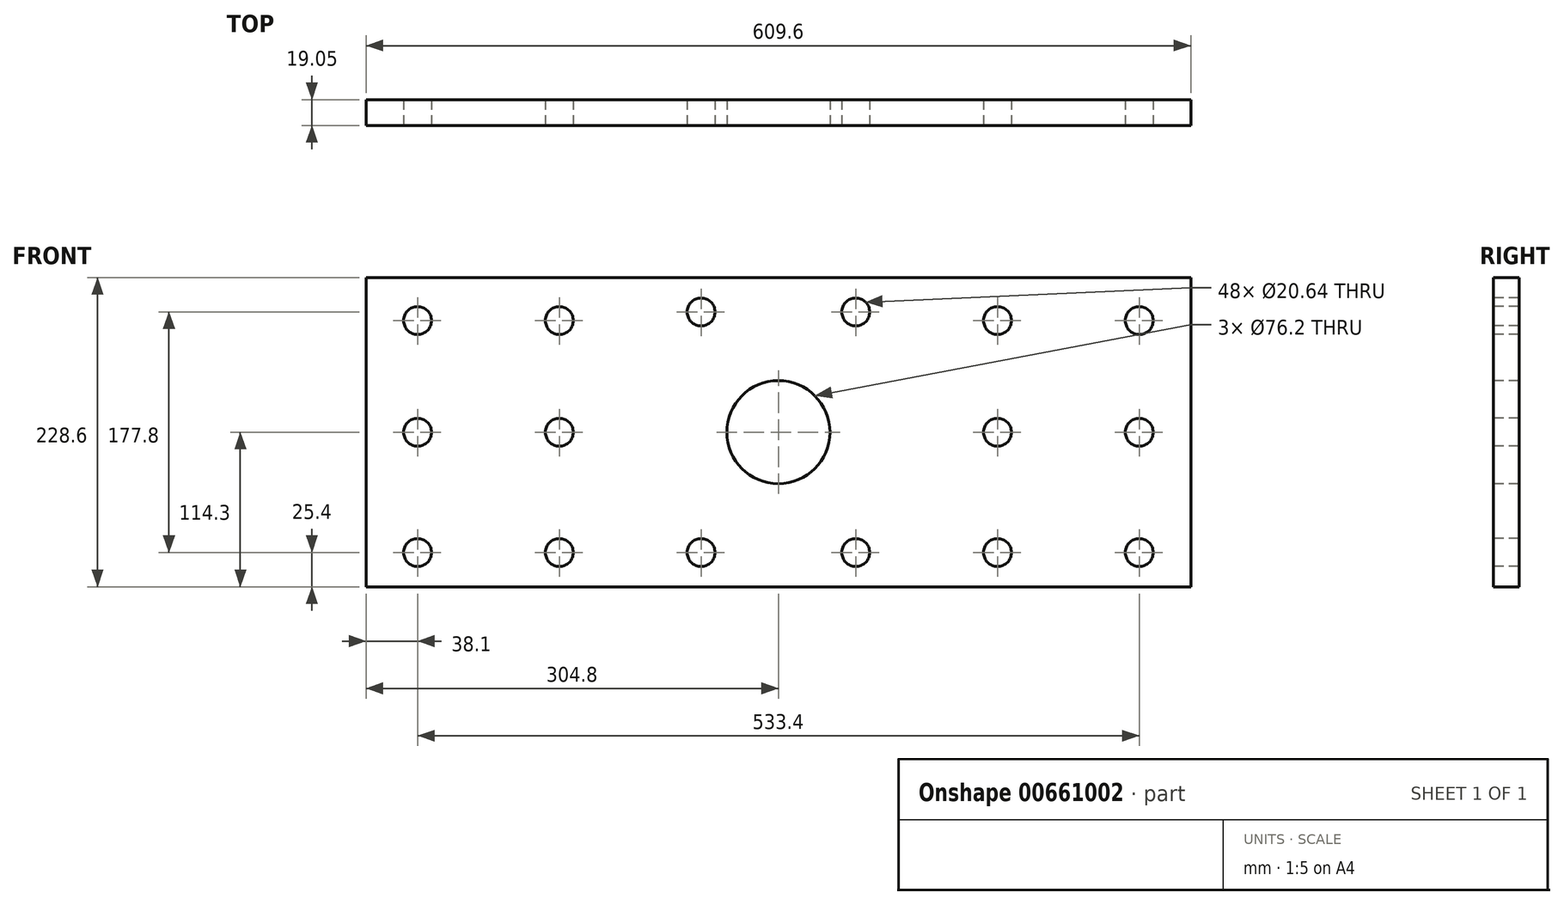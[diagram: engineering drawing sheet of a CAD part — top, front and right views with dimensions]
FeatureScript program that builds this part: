
annotation { "Feature Type Name" : "Feature", "Feature Type Description" : "" }
export const myFeature = defineFeature(function(context is Context, id is Id, definition is map)
    precondition{}
    {
        {
            var Q0;
            Q0=qCreatedBy(makeId("Front.planeOp"),FACE);
            var sketch = newSketch(context, id + "F0", { "sketchPlane" : qUnion([Q0])});
            skLineSegment(sketch, "E0", {"start": v(0, 0) * mm, "end": v(-609.6, 0) * mm, "construction": true});
            skLineSegment(sketch, "E1", {"start": v(0, 0) * mm, "end": v(0, 38.1) * mm, "construction": true});
            skCircle(sketch, "E2", {"center": v(0, 38.1) * mm, "radius": 38.1 * mm});
            skArc(sketch, "E3", {"start": v(-31.6, 85.72) * mm, "mid": v(0, -19.05) * mm, "end": v(31.6, 85.72) * mm});
            skCircle(sketch, "E4", {"center": v(161.93, 38.1) * mm, "radius": 10.32 * mm});
            skCircle(sketch, "E5", {"center": v(266.7, 38.1) * mm, "radius": 10.32 * mm});
            skCircle(sketch, "E6", {"center": v(161.93, -50.8) * mm, "radius": 10.32 * mm});
            skCircle(sketch, "E7", {"center": v(266.7, -50.8) * mm, "radius": 10.32 * mm});
            skCircle(sketch, "E8", {"center": v(57.15, 127) * mm, "radius": 10.32 * mm});
            skCircle(sketch, "E9", {"center": v(161.93, 120.65) * mm, "radius": 10.32 * mm});
            skCircle(sketch, "E10", {"center": v(266.7, 120.65) * mm, "radius": 10.32 * mm});
            skCircle(sketch, "E11", {"center": v(57.15, -50.8) * mm, "radius": 10.32 * mm});
            skLineSegment(sketch, "E12", {"start": v(0, 0) * mm, "end": v(0, 368.3) * mm, "construction": true});
            skCircle(sketch, "E13.MirrorC", {"center": v(-57.15, 127) * mm, "radius": 10.32 * mm});
            skCircle(sketch, "E14.MirrorC", {"center": v(-161.93, 120.65) * mm, "radius": 10.32 * mm});
            skCircle(sketch, "E15.MirrorC", {"center": v(-266.7, 120.65) * mm, "radius": 10.32 * mm});
            skCircle(sketch, "E16.MirrorC", {"center": v(-266.7, 38.1) * mm, "radius": 10.32 * mm});
            skCircle(sketch, "E17.MirrorC", {"center": v(-161.93, 38.1) * mm, "radius": 10.32 * mm});
            skCircle(sketch, "E18.MirrorC", {"center": v(-266.7, -50.8) * mm, "radius": 10.32 * mm});
            skCircle(sketch, "E19.MirrorC", {"center": v(-161.93, -50.8) * mm, "radius": 10.32 * mm});
            skCircle(sketch, "E20.MirrorC", {"center": v(-57.15, -50.8) * mm, "radius": 10.32 * mm});
            skLineSegment(sketch, "E21.bottom", {"start": v(304.8, 152.4) * mm, "end": v(-304.8, 152.4) * mm});
            skLineSegment(sketch, "E21.top", {"start": v(304.8, -76.2) * mm, "end": v(-304.8, -76.2) * mm});
            skLineSegment(sketch, "E21.left", {"start": v(304.8, 152.4) * mm, "end": v(304.8, 95.25) * mm});
            skLineSegment(sketch, "E21.right", {"start": v(-304.8, 152.4) * mm, "end": v(-304.8, -76.2) * mm});
            skLineSegment(sketch, "E22", {"start": v(0, 0) * mm, "end": v(609.6, 0) * mm, "construction": true});
            skLineSegment(sketch, "E23", {"start": v(0, 0) * mm, "end": v(0, 85.73) * mm, "construction": true});
            skLineSegment(sketch, "E24", {"start": v(0, 85.73) * mm, "end": v(31.6, 85.73) * mm});
            skLineSegment(sketch, "E25", {"start": v(0, 85.73) * mm, "end": v(-508, 85.73) * mm});
            skLineSegment(sketch, "E26", {"start": v(0, 85.73) * mm, "end": v(0, 95.25) * mm, "construction": true});
            skLineSegment(sketch, "E27", {"start": v(0, 95.25) * mm, "end": v(533.4, 95.25) * mm});
            skLineSegment(sketch, "E28", {"start": v(0, 95.25) * mm, "end": v(-508, 95.25) * mm});
            skLineSegment(sketch, "E29.left", {"start": v(660.4, -107.95) * mm, "end": v(660.4, 107.95) * mm});
            skLineSegment(sketch, "E29.right", {"start": v(558.8, -107.95) * mm, "end": v(558.8, 107.95) * mm});
            skLineSegment(sketch, "E30", {"start": v(660.4, 107.95) * mm, "end": v(676.27, 107.95) * mm});
            skLineSegment(sketch, "E31", {"start": v(676.27, 107.95) * mm, "end": v(676.27, 73.03) * mm});
            skLineSegment(sketch, "E32", {"start": v(676.27, -107.95) * mm, "end": v(660.4, -107.95) * mm});
            skLineSegment(sketch, "E33", {"start": v(558.8, 107.95) * mm, "end": v(542.92, 107.95) * mm});
            skLineSegment(sketch, "E34", {"start": v(542.92, 107.95) * mm, "end": v(542.92, 104.78) * mm});
            skLineSegment(sketch, "E35", {"start": v(542.92, -107.95) * mm, "end": v(558.8, -107.95) * mm});
            skLineSegment(sketch, "E36", {"start": v(0, 0) * mm, "end": v(0, -165.1) * mm, "construction": true});
            skLineSegment(sketch, "E37", {"start": v(0, -165.1) * mm, "end": v(685.18, -165.1) * mm});
            skLineSegment(sketch, "E38", {"start": v(0, 368.3) * mm, "end": v(152.4, 368.3) * mm, "construction": true});
            skCircle(sketch, "E39", {"center": v(152.4, 368.3) * mm, "radius": 11.9 * mm});
            skCircle(sketch, "E40", {"center": v(152.4, 368.3) * mm, "radius": 25.4 * mm});
            skLineSegment(sketch, "E41.bottom", {"start": v(609.6, 0) * mm, "end": v(671.5, 0) * mm, "construction": true});
            skLineSegment(sketch, "E41.top", {"start": v(609.6, 120.65) * mm, "end": v(671.5, 120.65) * mm, "construction": true});
            skLineSegment(sketch, "E41.left", {"start": v(609.6, 0) * mm, "end": v(609.6, 120.65) * mm, "construction": true});
            skLineSegment(sketch, "E41.right", {"start": v(671.5, 0) * mm, "end": v(671.5, 120.65) * mm, "construction": true});
            skArc(sketch, "E42", {"start": v(746.55, 107.42) * mm, "mid": v(736.68, 160.14) * mm, "end": v(694.5, 193.3) * mm});
            skLineSegment(sketch, "E43", {"start": v(700.81, -151.98) * mm, "end": v(746.55, 107.42) * mm});
            skPoint(sketch, "E44.visualSharp", {"position": v(698.5, -165.1) * mm});
            skArc(sketch, "E44.filletArc", {"start": v(685.18, -165.1) * mm, "mid": v(695.38, -161.39) * mm, "end": v(700.81, -151.98) * mm});
            skLineSegment(sketch, "E45", {"start": v(0, 368.3) * mm, "end": v(0, 381) * mm, "construction": true});
            skLineSegment(sketch, "E46", {"start": v(0, 381) * mm, "end": v(93.75, 381) * mm});
            skLineSegment(sketch, "E47", {"start": v(109.08, 378.63) * mm, "end": v(127.4, 372.83) * mm});
            skLineSegment(sketch, "E48.trimOffspring", {"start": v(175.45, 357.62) * mm, "end": v(694.5, 193.3) * mm});
            skLineSegment(sketch, "E49.trimOffspring", {"start": v(140.5, 368.69) * mm, "end": v(141.72, 368.3) * mm});
            skPoint(sketch, "E50.visualSharp", {"position": v(101.6, 381) * mm});
            skArc(sketch, "E50.filletArc", {"start": v(109.08, 378.63) * mm, "mid": v(101.5, 380.4) * mm, "end": v(93.75, 381) * mm});
            skLineSegment(sketch, "E51.bottom", {"start": v(685.8, 44.45) * mm, "end": v(533.4, 44.45) * mm, "construction": true});
            skLineSegment(sketch, "E51.top", {"start": v(685.8, -44.45) * mm, "end": v(533.4, -44.45) * mm, "construction": true});
            skLineSegment(sketch, "E51.left", {"start": v(685.8, 44.45) * mm, "end": v(685.8, -44.45) * mm, "construction": true});
            skLineSegment(sketch, "E51.right", {"start": v(533.4, 44.45) * mm, "end": v(533.4, -44.45) * mm, "construction": true});
            skCircle(sketch, "E52", {"center": v(533.4, 44.45) * mm, "radius": 6.6 * mm});
            skCircle(sketch, "E53", {"center": v(533.4, -44.45) * mm, "radius": 6.6 * mm});
            skCircle(sketch, "E54", {"center": v(685.8, 44.45) * mm, "radius": 6.6 * mm});
            skCircle(sketch, "E55", {"center": v(685.8, -44.45) * mm, "radius": 6.6 * mm});
            skArc(sketch, "E56", {"start": v(533.4, 63.5) * mm, "mid": v(514.35, 44.45) * mm, "end": v(533.4, 25.4) * mm});
            skArc(sketch, "E57", {"start": v(685.8, 25.4) * mm, "mid": v(704.85, 44.45) * mm, "end": v(685.8, 63.5) * mm});
            skArc(sketch, "E58", {"start": v(685.8, -63.5) * mm, "mid": v(704.85, -44.45) * mm, "end": v(685.8, -25.4) * mm});
            skArc(sketch, "E59", {"start": v(533.4, -25.4) * mm, "mid": v(514.35, -44.45) * mm, "end": v(533.4, -63.5) * mm});
            skLineSegment(sketch, "E60.trimOffspring", {"start": v(542.92, 15.88) * mm, "end": v(542.92, -15.87) * mm});
            skLineSegment(sketch, "E61.trimOffspring", {"start": v(542.92, -73.02) * mm, "end": v(542.92, -107.95) * mm});
            skPoint(sketch, "E62.visualSharp", {"position": v(542.92, 27.95) * mm});
            skArc(sketch, "E62.filletArc", {"start": v(542.93, 15.88) * mm, "mid": v(540.14, 22.61) * mm, "end": v(533.4, 25.4) * mm});
            skPoint(sketch, "E63.visualSharp", {"position": v(542.92, 60.95) * mm});
            skArc(sketch, "E63.filletArc", {"start": v(533.4, 63.5) * mm, "mid": v(540.14, 66.29) * mm, "end": v(542.92, 73.03) * mm});
            skPoint(sketch, "E64.visualSharp", {"position": v(542.92, -27.95) * mm});
            skArc(sketch, "E64.filletArc", {"start": v(533.4, -25.4) * mm, "mid": v(540.14, -22.61) * mm, "end": v(542.92, -15.87) * mm});
            skPoint(sketch, "E65.visualSharp", {"position": v(542.92, -60.95) * mm});
            skArc(sketch, "E65.filletArc", {"start": v(542.92, -73.02) * mm, "mid": v(540.14, -66.29) * mm, "end": v(533.4, -63.5) * mm});
            skLineSegment(sketch, "E66.trimOffspring", {"start": v(676.27, 15.88) * mm, "end": v(676.27, -15.87) * mm});
            skLineSegment(sketch, "E67.trimOffspring", {"start": v(676.27, -73.02) * mm, "end": v(676.27, -107.95) * mm});
            skPoint(sketch, "E68.visualSharp", {"position": v(676.27, 60.95) * mm});
            skArc(sketch, "E68.filletArc", {"start": v(676.27, 73.03) * mm, "mid": v(679.06, 66.29) * mm, "end": v(685.8, 63.5) * mm});
            skPoint(sketch, "E69.visualSharp", {"position": v(676.27, 27.95) * mm});
            skArc(sketch, "E69.filletArc", {"start": v(685.8, 25.4) * mm, "mid": v(679.06, 22.61) * mm, "end": v(676.27, 15.88) * mm});
            skPoint(sketch, "E70.visualSharp", {"position": v(676.27, -27.95) * mm});
            skArc(sketch, "E70.filletArc", {"start": v(676.27, -15.87) * mm, "mid": v(679.06, -22.61) * mm, "end": v(685.8, -25.4) * mm});
            skPoint(sketch, "E71.visualSharp", {"position": v(676.27, -60.95) * mm});
            skArc(sketch, "E71.filletArc", {"start": v(685.8, -63.5) * mm, "mid": v(679.06, -66.29) * mm, "end": v(676.27, -73.02) * mm});
            skLineSegment(sketch, "E72", {"start": v(542.92, 73.03) * mm, "end": v(542.92, 15.88) * mm});
            skLineSegment(sketch, "E73", {"start": v(676.27, 73.03) * mm, "end": v(676.27, 15.88) * mm});
            skLineSegment(sketch, "E74", {"start": v(676.27, -15.87) * mm, "end": v(676.27, -73.02) * mm});
            skLineSegment(sketch, "E75", {"start": v(542.92, -15.87) * mm, "end": v(542.92, -73.02) * mm});
            skLineSegment(sketch, "E76.trimOffspring", {"start": v(542.92, 76.2) * mm, "end": v(542.92, 73.03) * mm});
            skPoint(sketch, "E77.visualSharp", {"position": v(542.92, 95.25) * mm});
            skArc(sketch, "E77.filletArc", {"start": v(533.4, 95.25) * mm, "mid": v(540.14, 98.04) * mm, "end": v(542.92, 104.78) * mm});
            skPoint(sketch, "E78.visualSharp", {"position": v(542.92, 85.73) * mm});
            skArc(sketch, "E78.filletArc", {"start": v(542.92, 76.2) * mm, "mid": v(540.14, 82.94) * mm, "end": v(533.4, 85.73) * mm});
            skLineSegment(sketch, "E79.trimOffspring", {"start": v(304.8, 95.25) * mm, "end": v(304.8, -76.2) * mm});
            skLineSegment(sketch, "E80.trimOffspring", {"start": v(342.9, 85.73) * mm, "end": v(450.85, 85.73) * mm});
            skPoint(sketch, "E81.visualSharp", {"position": v(304.8, 85.73) * mm});
            skArc(sketch, "E81.filletArc", {"start": v(342.9, 85.72) * mm, "mid": v(315.96, 74.57) * mm, "end": v(304.8, 47.62) * mm});
            skLineSegment(sketch, "E82", {"start": v(304.8, -76.2) * mm, "end": v(304.8, -76.2) * mm});
            skLineSegment(sketch, "E83", {"start": v(342.9, -114.3) * mm, "end": v(450.85, -114.3) * mm});
            skLineSegment(sketch, "E84", {"start": v(488.95, -76.2) * mm, "end": v(488.95, 47.63) * mm});
            skPoint(sketch, "E85.visualSharp", {"position": v(488.95, 85.73) * mm});
            skArc(sketch, "E85.filletArc", {"start": v(488.95, 47.63) * mm, "mid": v(477.8, 74.57) * mm, "end": v(450.85, 85.72) * mm});
            skPoint(sketch, "E86.visualSharp", {"position": v(488.95, -114.3) * mm});
            skArc(sketch, "E86.filletArc", {"start": v(450.85, -114.3) * mm, "mid": v(477.8, -103.14) * mm, "end": v(488.95, -76.2) * mm});
            skPoint(sketch, "E87.visualSharp", {"position": v(304.8, -114.3) * mm});
            skArc(sketch, "E87.filletArc", {"start": v(304.8, -76.2) * mm, "mid": v(315.96, -103.14) * mm, "end": v(342.9, -114.3) * mm});
            skLineSegment(sketch, "E88", {"start": v(498.48, -76.2) * mm, "end": v(498.48, 76.2) * mm});
            skLineSegment(sketch, "E89", {"start": v(508, 85.73) * mm, "end": v(533.4, 85.73) * mm});
            skLineSegment(sketch, "E90", {"start": v(295.28, -76.2) * mm, "end": v(295.28, 76.2) * mm});
            skArc(sketch, "E91", {"start": v(295.28, -76.2) * mm, "mid": v(309.22, -109.88) * mm, "end": v(342.9, -123.83) * mm});
            skArc(sketch, "E92", {"start": v(498.48, -76.2) * mm, "mid": v(484.53, -109.88) * mm, "end": v(450.85, -123.83) * mm});
            skLineSegment(sketch, "E93", {"start": v(342.9, -123.83) * mm, "end": v(450.85, -123.83) * mm});
            skLineSegment(sketch, "E94", {"start": v(342.9, 85.72) * mm, "end": v(285.75, 85.72) * mm});
            skLineSegment(sketch, "E95.trimOffspring", {"start": v(285.75, 85.72) * mm, "end": v(31.6, 85.72) * mm});
            skPoint(sketch, "E96.visualSharp", {"position": v(295.28, 85.72) * mm});
            skArc(sketch, "E96.filletArc", {"start": v(295.28, 76.2) * mm, "mid": v(292.49, 82.94) * mm, "end": v(285.75, 85.72) * mm});
            skPoint(sketch, "E97.visualSharp", {"position": v(498.48, 85.72) * mm});
            skArc(sketch, "E97.filletArc", {"start": v(508, 85.73) * mm, "mid": v(501.26, 82.94) * mm, "end": v(498.48, 76.2) * mm});
            skLineSegment(sketch, "E98.bottom", {"start": v(609.6, 0) * mm, "end": v(555.62, 0) * mm, "construction": true});
            skLineSegment(sketch, "E98.top", {"start": v(609.6, 120.65) * mm, "end": v(555.62, 120.65) * mm, "construction": true});
            skLineSegment(sketch, "E98.right", {"start": v(555.62, 0) * mm, "end": v(555.62, 120.65) * mm, "construction": true});
            skArc(sketch, "E99", {"start": v(555.62, 196.85) * mm, "mid": v(497.95, 170.45) * mm, "end": v(480.24, 109.54) * mm});
            skLineSegment(sketch, "E100", {"start": v(609.6, -165.1) * mm, "end": v(520.7, -165.1) * mm, "construction": true});
            skPoint(sketch, "E100.startSnap0", {"position": v(609.6, -44.45) * mm});
            skLineSegment(sketch, "E101", {"start": v(520.7, -165.1) * mm, "end": v(480.24, 109.54) * mm});
            skLineSegment(sketch, "E102", {"start": v(555.62, 196.85) * mm, "end": v(683.28, 196.85) * mm});
            skArc(sketch, "E103.trimOffspring", {"start": v(555.62, 44.45) * mm, "mid": v(557.21, 44.47) * mm, "end": v(558.8, 44.52) * mm});
            skSolve(sketch);
        }
        {
            var Q0;
            Q0=makeQuery(id+"F0.imprint","IMPRINT",FACE,{"disambiguationData":[TD([[makeQuery(id+"F0.imprint","IMPRINT",EDGE,{"derivedFrom":sQuery(id+"F0.wireOp",EDGE,"E3")}),-1.0]])]});
            var Q1;
            Q1=makeQuery(id+"F0.imprint","IMPRINT",FACE,{"disambiguationData":[TD([[makeQuery(id+"F0.imprint","IMPRINT",EDGE,{"derivedFrom":sQuery(id+"F0.wireOp",EDGE,"E2")}),-1.0]])]});
            var Q2;
            Q2=makeQuery(id+"F0.imprint","IMPRINT",FACE,{"disambiguationData":[TD([[makeQuery(id+"F0.imprint","IMPRINT",EDGE,{"derivedFrom":sQuery(id+"F0.wireOp",EDGE,"E8")}),-1.0]])]});
            var Q3;
            {var subQ3=sQuery(id+"F0.wireOp",EDGE,"E21.left");var subQ11=sQuery(id+"F0.wireOp",EDGE,"E27");var subQ12=makeQuery(id+"F0.imprint","INTERSECT",VERTEX,{"derivedFrom":[subQ3,subQ11]});Q3=makeQuery(id+"F0.imprint","IMPRINT",FACE,{"disambiguationData":[TD([[makeQuery(id+"F0.imprint","IMPRINT",EDGE,{"disambiguationData":[TD([[subQ12,-1.0]])],"derivedFrom":subQ3}),-1.0]])]});}
            var Q4;
            {var subQ4=sQuery(id+"F0.wireOp",EDGE,"E24");Q4=makeQuery(id+"F0.imprint","IMPRINT",FACE,{"disambiguationData":[TD([[makeQuery(id+"F0.imprint","IMPRINT",EDGE,{"derivedFrom":subQ4}),1.0]])]});}
            var Q5;
            {var subQ0=sQuery(id+"F0.wireOp",EDGE,"E90");Q5=makeQuery(id+"F0.imprint","IMPRINT",FACE,{"disambiguationData":[TD([[makeQuery(id+"F0.imprint","IMPRINT",EDGE,{"derivedFrom":subQ0}),-1.0]])]});}
            extrude(context, id + "F1", {"entities" : qUnion([Q0, Q1, Q2, Q3, Q4, Q5]), "oppositeDirection" : true, "depth" : 19.05 * mm, "offsetDistance" : 25.4 * mm});
        }
    });
